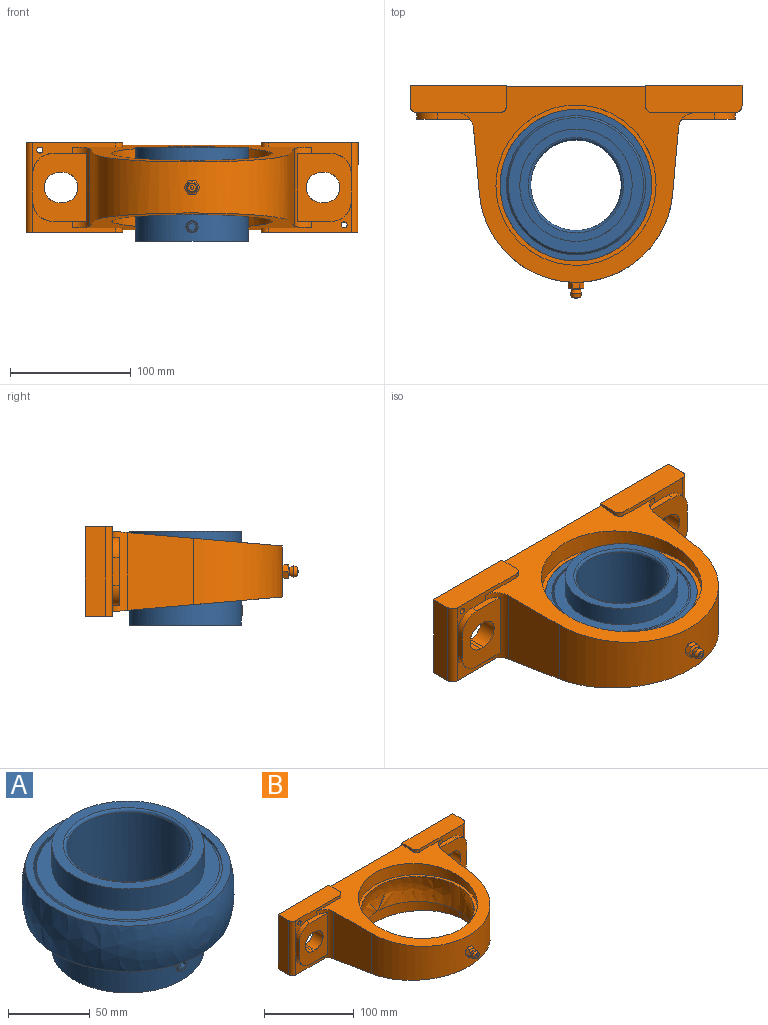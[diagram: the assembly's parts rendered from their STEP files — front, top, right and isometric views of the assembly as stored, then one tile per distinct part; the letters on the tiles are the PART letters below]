
ASSEMBLY  parts=2 mates=1
PART A: 143 faces, bbox 127.1x129.4x131.6 mm
  f0: plane 7.1x6.16mm, normal (0.87,0.5,0), area 38.5mm2, adj f1
  f1: cone r=1.71mm half-angle=45deg, axis (0.87,0.5,0), area 56.6mm2, adj f0,f2
  f2: cylinder r=5mm len=10.05mm, axis (0.87,0.5,0), area 79.3mm2, adj f1,f3
  f3: cylinder r=37.5mm len=75mm, axis (0,0,1), area 17220.6mm2, adj f2,f4,f139,f142
  f4: torus R=39.5mm, axis (0,0,-1), area 754.6mm2, adj f3,f5
  f5: plane 93.01x93.01mm, normal (0,0,-1), area 1887mm2, adj f4,f6
  f6: cylinder r=46.5mm len=93mm, axis (0,0,-1), area 7783.3mm2, adj f5,f7,f105,f106,f107,f108,f109,f110
  f7: sphere r=8.34mm, area 847.9mm2, adj f6,f8,f9,f10,f53,f54,f55,f56
  f8: torus R=51.49mm, axis (0,0,1), area 160.7mm2, adj f7,f9,f95,f106
  f9: torus R=51.49mm, axis (0,0,1), area 160.7mm2, adj f7,f8,f10,f106
  f10: cylinder r=56.49mm len=112.98mm, axis (0,0,1), area 2460.6mm2, adj f7,f9,f11,f13,f15,f17,f19,f21
  f11: torus R=51.49mm, axis (0,0,1), area 160.8mm2, adj f10,f12,f118,f120
  f12: torus R=51.49mm, axis (0,0,1), area 160.7mm2, adj f11,f95,f118,f120
  f13: torus R=51.49mm, axis (0,0,1), area 160.7mm2, adj f10,f14,f116,f118
  f14: torus R=51.49mm, axis (0,0,1), area 160.7mm2, adj f13,f95,f116,f118
  f15: torus R=51.49mm, axis (0,0,1), area 160.7mm2, adj f10,f16,f114,f116
  f16: torus R=51.49mm, axis (0,0,1), area 160.7mm2, adj f15,f95,f114,f116
  f17: torus R=51.49mm, axis (0,0,1), area 160.7mm2, adj f10,f18,f112,f114
  f18: torus R=51.49mm, axis (0,0,1), area 160.7mm2, adj f17,f95,f112,f114
  f19: torus R=51.49mm, axis (0,0,1), area 160.7mm2, adj f10,f20,f110,f112
  f20: torus R=51.49mm, axis (0,0,1), area 160.7mm2, adj f19,f95,f110,f112
  f21: torus R=51.49mm, axis (0,0,1), area 81.7mm2, adj f10,f22,f24,f110
  f22: torus R=51.49mm, axis (0,0,1), area 81.7mm2, adj f21,f23,f95,f110
  f23: torus R=51.49mm, axis (0,0,1), area 78.9mm2, adj f22,f24,f95,f108
  f24: torus R=51.49mm, axis (0,0,1), area 79mm2, adj f10,f21,f23,f108
  f25: torus R=51.49mm, axis (0,0,1), area 160.7mm2, adj f10,f26,f106,f108
  f26: torus R=51.49mm, axis (0,0,1), area 160.7mm2, adj f25,f95,f106,f108
  f27: torus R=51.49mm, axis (0,0,1), area 160.7mm2, adj f10,f28,f135,f137
  f28: torus R=51.49mm, axis (0,0,1), area 160.7mm2, adj f27,f95,f135,f137
  f29: torus R=51.49mm, axis (0,0,1), area 160.7mm2, adj f10,f30,f133,f135
  f30: torus R=51.49mm, axis (0,0,1), area 160.7mm2, adj f29,f95,f133,f135
  f31: torus R=51.49mm, axis (0,0,1), area 160.7mm2, adj f10,f32,f131,f133
  f32: torus R=51.49mm, axis (0,0,1), area 160.7mm2, adj f31,f95,f131,f133
  f33: torus R=51.49mm, axis (0,0,1), area 160.7mm2, adj f10,f34,f129,f131
  f34: torus R=51.49mm, axis (0,0,1), area 160.7mm2, adj f33,f95,f129,f131
  f35: torus R=51.49mm, axis (0,0,1), area 160.7mm2, adj f10,f36,f127,f129
  f36: torus R=51.49mm, axis (0,0,1), area 160.7mm2, adj f35,f95,f127,f129
  f37: torus R=51.49mm, axis (0,0,1), area 160.7mm2, adj f10,f38,f124,f127
  f38: torus R=51.49mm, axis (0,0,1), area 160.7mm2, adj f37,f95,f124,f127
  f39: torus R=51.49mm, axis (0,0,1), area 160.8mm2, adj f10,f40,f122,f124
  f40: torus R=51.49mm, axis (0,0,1), area 160.7mm2, adj f39,f95,f122,f124
  f41: torus R=51.49mm, axis (0,0,1), area 160.8mm2, adj f10,f42,f120,f122
  f42: torus R=51.49mm, axis (0,0,1), area 160.7mm2, adj f41,f95,f120,f122
  f43: cylinder r=0.87mm len=9.02mm, axis (0,-0.97,0.26), area 45.2mm2, adj f10,f44
  f44: sphere r=65mm, area 19597mm2, adj f43,f45
  f45: plane 125.48x125.48mm, normal (0,0,1), area 1907.7mm2, adj f44,f46
  f46: cylinder r=57.62mm len=115.24mm, axis (0,0,1), area 611.8mm2, adj f45,f47
  f47: cone r=55.93mm half-angle=45deg, axis (0,0,1), area 852.6mm2, adj f46,f48
  f48: plane 113.5x113.5mm, normal (0,0,1), area 3025.4mm2, adj f47,f49
  f49: cylinder r=46.51mm len=93.02mm, axis (0,0,-1), area 990.7mm2, adj f48,f50
  f50: plane 115.25x115.25mm, normal (0,0,-1), area 3627.1mm2, adj f49,f51
  f51: cylinder r=57.62mm len=115.24mm, axis (0,0,1), area 3.6mm2, adj f50,f52
  f52: plane 115.25x115.25mm, normal (0,0,1), area 412mm2, adj f10,f51
  f53: torus R=51.49mm, axis (0,0,1), area 160.7mm2, adj f7,f10,f54,f137
  f54: torus R=51.49mm, axis (0,0,1), area 160.7mm2, adj f7,f53,f95,f137
  f55: torus R=51.49mm, axis (0,0,1), area 120.6mm2, adj f7,f56,f137,f138
  f56: cylinder r=46.5mm len=93mm, axis (0,0,-1), area 10888.8mm2, adj f7,f55,f57,f67,f68,f69,f70,f71
  f57: cylinder r=5mm len=10mm, axis (-0.87,-0.5,0), area 4.9mm2, adj f56,f58
  f58: cone r=2.14mm half-angle=45deg, axis (-0.87,-0.5,0), area 37.1mm2, adj f57,f59
  f59: plane 8.28x7.19mm, normal (-0.87,-0.5,0), area 30.7mm2, adj f58,f60,f62,f63,f64,f65,f66
  f60: plane 5.58x4.67mm, normal (-0.25,0.43,0.87), area 14.4mm2, adj f59,f61,f62,f66
  f61: plane 5.77x4.33mm, normal (-0.87,-0.5,0), area 21.7mm2, adj f60,f62,f63,f64,f65,f66
  f62: plane 5.58x4.67mm, normal (0.25,-0.43,0.87), area 14.4mm2, adj f59,f60,f61,f63
  f63: plane 4.33x2.89mm, normal (0.5,-0.87,0), area 14.4mm2, adj f59,f61,f62,f64
  f64: plane 5.58x4.67mm, normal (0.25,-0.43,-0.87), area 14.4mm2, adj f59,f61,f63,f65
  f65: plane 5.58x4.67mm, normal (-0.25,0.43,-0.87), area 14.4mm2, adj f59,f61,f64,f66
  f66: plane 4.33x2.89mm, normal (-0.5,0.87,0), area 14.4mm2, adj f59,f60,f61,f65
  f67: torus R=51.49mm, axis (0,0,1), area 120.6mm2, adj f56,f118,f119,f120
  f68: torus R=51.49mm, axis (0,0,1), area 120.6mm2, adj f56,f116,f117,f118
  f69: torus R=51.49mm, axis (0,0,1), area 120.6mm2, adj f56,f114,f115,f116
  f70: torus R=51.49mm, axis (0,0,1), area 120.6mm2, adj f56,f112,f113,f114
  f71: torus R=51.49mm, axis (0,0,1), area 120.6mm2, adj f56,f110,f111,f112
  f72: torus R=51.49mm, axis (0,0,1), area 120.6mm2, adj f56,f108,f109,f110
  f73: torus R=51.49mm, axis (0,0,1), area 120.6mm2, adj f56,f106,f107,f108
  f74: torus R=51.49mm, axis (0,0,1), area 120.6mm2, adj f56,f135,f136,f137
  f75: torus R=51.49mm, axis (0,0,1), area 120.6mm2, adj f56,f133,f134,f135
  f76: torus R=51.49mm, axis (0,0,1), area 120.6mm2, adj f56,f131,f132,f133
  f77: torus R=51.49mm, axis (0,0,1), area 120.6mm2, adj f56,f129,f130,f131
  f78: torus R=51.49mm, axis (0,0,1), area 120.6mm2, adj f56,f127,f128,f129
  f79: torus R=51.49mm, axis (0,0,1), area 59.1mm2, adj f56,f80,f126,f127
  f80: torus R=51.49mm, axis (0,0,1), area 61.5mm2, adj f56,f79,f124,f125
  f81: torus R=51.49mm, axis (0,0,1), area 120.6mm2, adj f56,f122,f123,f124
  f82: torus R=51.49mm, axis (0,0,1), area 120.6mm2, adj f56,f120,f121,f122
  f83: plane 93.01x93.01mm, normal (0,0,1), area 1887mm2, adj f56,f142
  f84: cylinder r=5mm len=10mm, axis (0,1,0), area 4.9mm2, adj f56,f85
  f85: cone r=4.08mm half-angle=45deg, axis (0,1,0), area 37.1mm2, adj f84,f86
  f86: plane 8.28x8.28mm, normal (0,1,0), area 30.7mm2, adj f85,f87,f89,f90,f91,f92,f93
  f87: plane 5x2.5mm, normal (0.5,0,0.87), area 14.4mm2, adj f86,f88,f89,f93
  f88: plane 5.77x5mm, normal (0,1,0), area 21.7mm2, adj f87,f89,f90,f91,f92,f93
  f89: plane 5x2.5mm, normal (-0.5,0,0.87), area 14.4mm2, adj f86,f87,f88,f90
  f90: plane 5x2.89mm, normal (-1,0,0), area 14.4mm2, adj f86,f88,f89,f91
  f91: plane 5x2.5mm, normal (-0.5,0,-0.87), area 14.4mm2, adj f86,f88,f90,f92
  f92: plane 5x2.5mm, normal (0.5,0,-0.87), area 14.4mm2, adj f86,f88,f91,f93
  f93: plane 5x2.89mm, normal (1,0,0), area 14.4mm2, adj f86,f87,f88,f92
  f94: torus R=51.49mm, axis (0,0,1), area 120.6mm2, adj f7,f56,f105,f106
  f95: cylinder r=56.49mm len=112.98mm, axis (0,0,1), area 2463.2mm2, adj f7,f8,f12,f14,f16,f18,f20,f22
  f96: plane 115.25x115.25mm, normal (0,0,-1), area 397.7mm2, adj f95,f97
  f97: cylinder r=57.62mm len=115.24mm, axis (0,0,1), area 3.6mm2, adj f96,f98
  f98: plane 116.6x116.6mm, normal (0,0,1), area 3638.6mm2, adj f97,f99
  f99: cylinder r=46.51mm len=93.02mm, axis (0,0,1), area 990.7mm2, adj f98,f100
  f100: plane 113.5x113.5mm, normal (0,0,-1), area 3025.4mm2, adj f99,f101
  f101: cone r=55.93mm half-angle=45deg, axis (0,0,-1), area 852.6mm2, adj f100,f102
  f102: cylinder r=57.62mm len=115.24mm, axis (0,0,1), area 611.8mm2, adj f101,f103
  f103: plane 125.48x125.48mm, normal (0,0,-1), area 1909mm2, adj f102,f104
  f104: sphere r=65mm, area 19599.5mm2, adj f103
  f105: torus R=51.49mm, axis (0,0,1), area 120.6mm2, adj f6,f7,f94,f106
  f106: sphere r=8.34mm, area 847.9mm2, adj f6,f8,f9,f10,f25,f26,f56,f73
  f107: torus R=51.49mm, axis (0,0,1), area 120.6mm2, adj f6,f73,f106,f108
  f108: sphere r=8.34mm, area 847.9mm2, adj f6,f10,f23,f24,f25,f26,f56,f72
  f109: torus R=51.49mm, axis (0,0,1), area 120.6mm2, adj f6,f72,f108,f110
  f110: sphere r=8.34mm, area 847.9mm2, adj f6,f10,f19,f20,f21,f22,f56,f71
  f111: torus R=51.49mm, axis (0,0,1), area 120.6mm2, adj f6,f71,f110,f112
  f112: sphere r=8.34mm, area 847.9mm2, adj f6,f10,f17,f18,f19,f20,f56,f70
  f113: torus R=51.49mm, axis (0,0,1), area 120.6mm2, adj f6,f70,f112,f114
  f114: sphere r=8.34mm, area 847.9mm2, adj f6,f10,f15,f16,f17,f18,f56,f69
  f115: torus R=51.49mm, axis (0,0,1), area 120.6mm2, adj f6,f69,f114,f116
  f116: sphere r=8.34mm, area 847.9mm2, adj f6,f10,f13,f14,f15,f16,f56,f68
  f117: torus R=51.49mm, axis (0,0,1), area 120.6mm2, adj f6,f68,f116,f118
  f118: sphere r=8.34mm, area 847.9mm2, adj f6,f10,f11,f12,f13,f14,f56,f67
  f119: torus R=51.49mm, axis (0,0,1), area 120.6mm2, adj f6,f67,f118,f120
  f120: sphere r=8.34mm, area 847.9mm2, adj f6,f10,f11,f12,f41,f42,f56,f67
  f121: torus R=51.49mm, axis (0,0,1), area 120.6mm2, adj f6,f82,f120,f122
  f122: sphere r=8.34mm, area 847.9mm2, adj f6,f10,f39,f40,f41,f42,f56,f81
  f123: torus R=51.49mm, axis (0,0,1), area 120.6mm2, adj f6,f81,f122,f124
  f124: sphere r=8.34mm, area 847.9mm2, adj f6,f10,f37,f38,f39,f40,f56,f80
  f125: torus R=51.49mm, axis (0,0,1), area 61.5mm2, adj f6,f80,f124,f126
  f126: torus R=51.49mm, axis (0,0,1), area 59.1mm2, adj f6,f79,f125,f127
  f127: sphere r=8.34mm, area 847.9mm2, adj f6,f10,f35,f36,f37,f38,f56,f78
  f128: torus R=51.49mm, axis (0,0,1), area 120.6mm2, adj f6,f78,f127,f129
  f129: sphere r=8.34mm, area 847.9mm2, adj f6,f10,f33,f34,f35,f36,f56,f77
  f130: torus R=51.49mm, axis (0,0,1), area 120.6mm2, adj f6,f77,f129,f131
  f131: sphere r=8.34mm, area 847.9mm2, adj f6,f10,f31,f32,f33,f34,f56,f76
  f132: torus R=51.49mm, axis (0,0,1), area 120.6mm2, adj f6,f76,f131,f133
  f133: sphere r=8.34mm, area 847.9mm2, adj f6,f10,f29,f30,f31,f32,f56,f75
  f134: torus R=51.49mm, axis (0,0,1), area 120.6mm2, adj f6,f75,f133,f135
  f135: sphere r=8.34mm, area 847.9mm2, adj f6,f10,f27,f28,f29,f30,f56,f74
  f136: torus R=51.49mm, axis (0,0,1), area 120.6mm2, adj f6,f74,f135,f137
  f137: sphere r=8.34mm, area 847.9mm2, adj f6,f10,f27,f28,f53,f54,f55,f56
  f138: torus R=51.49mm, axis (0,0,1), area 120.6mm2, adj f6,f7,f55,f137
  f139: cylinder r=5mm len=10mm, axis (0,-1,0), area 79.3mm2, adj f3,f140
  f140: cone r=3.5mm half-angle=45deg, axis (0,-1,0), area 56.6mm2, adj f139,f141
  f141: plane 7.1x7.1mm, normal (0,-1,0), area 38.5mm2, adj f140
  f142: torus R=39.5mm, axis (0,0,-1), area 754.6mm2, adj f3,f83
PART B: 85 faces, bbox 315.1x216.6x170.1 mm
  f0: plane 65.39x49.89mm, normal (0,1,0), area 2651.8mm2, adj f8,f9,f10,f11,f13,f14,f15,f16
  f1: plane 65.39x49.89mm, normal (0,1,0), area 2651.8mm2, adj f3,f4,f5,f6,f18,f19,f20,f21
  f2: sphere r=65.01mm, area 12961.5mm2, adj f24,f27
  f3: plane 49.5x12.6mm, normal (1,0,0), area 623.7mm2, adj f1,f4,f6,f31
  f4: plane 65x12.6mm, normal (0,0,1), area 819mm2, adj f1,f3,f5,f31
  f5: plane 49.5x12.6mm, normal (-1,0,0), area 623.7mm2, adj f1,f4,f6,f31
  f6: plane 65x12.6mm, normal (0,0,-1), area 819mm2, adj f1,f3,f5,f31
  f7: plane 74x16.8mm, normal (1,0,0), area 1243.2mm2, adj f29,f30,f31,f32
  f8: plane 49.5x12.6mm, normal (1,0,0), area 623.7mm2, adj f0,f9,f11,f33
  f9: plane 65x12.6mm, normal (0,0,1), area 819mm2, adj f0,f8,f10,f33
  f10: plane 49.5x12.6mm, normal (-1,0,0), area 623.7mm2, adj f0,f9,f11,f33
  f11: plane 65x12.6mm, normal (0,0,-1), area 819mm2, adj f0,f8,f10,f33
  f12: plane 74x16.8mm, normal (-1,0,0), area 1243.2mm2, adj f33,f34,f35,f36
  f13: plane 15.4x3mm, normal (0,0,1), area 46.2mm2, adj f0,f14,f16,f39
  f14: cylinder r=12.5mm len=25mm, axis (0,-1,0), area 604.8mm2, adj f0,f13,f15,f39
  f15: plane 15.4x3mm, normal (0,0,-1), area 46.2mm2, adj f0,f14,f16,f39
  f16: cylinder r=12.5mm len=25mm, axis (0,-1,0), area 604.8mm2, adj f0,f13,f15,f39
  f17: plane 22.52x5.6mm, normal (-1,0,0), area 126.1mm2, adj f26,f36,f37,f39
  f18: plane 15.4x3mm, normal (0,0,1), area 46.2mm2, adj f1,f19,f21,f42
  f19: cylinder r=12.5mm len=25mm, axis (0,-1,0), area 604.8mm2, adj f1,f18,f20,f42
  f20: plane 15.4x3mm, normal (0,0,-1), area 46.2mm2, adj f1,f19,f21,f42
  f21: cylinder r=12.5mm len=25mm, axis (0,-1,0), area 604.8mm2, adj f1,f18,f20,f42
  f22: plane 22.52x5.6mm, normal (1,0,0), area 126.1mm2, adj f25,f28,f29,f42
  f23: sphere r=2.11mm, area 8.9mm2, adj f44
  f24: plane 172.74x172.74mm, normal (0,0,-1), area 1506mm2, adj f2,f45,f46
  f25: cylinder r=16.89mm len=16.89mm, axis (0,1,0), area 148.6mm2, adj f22,f41,f42,f47
  f26: cylinder r=16.89mm len=16.89mm, axis (0,1,0), area 148.6mm2, adj f17,f39,f40,f48
  f27: plane 172.74x172.74mm, normal (0,0,1), area 1506mm2, adj f2,f51
  f28: cylinder r=16.89mm len=16.89mm, axis (0,1,0), area 148.6mm2, adj f22,f42,f43,f52
  f29: cylinder r=5.6mm len=74mm, axis (0,0,1), area 650.9mm2, adj f7,f22,f30,f32,f47,f52
  f30: plane 80.35x22.75mm, normal (0,0,1), area 1778.7mm2, adj f7,f29,f31,f52,f53,f54
  f31: plane 80x74mm, normal (0,1,0), area 2682.9mm2, adj f3,f4,f5,f6,f7,f30,f32,f54
  f32: plane 80.35x22.75mm, normal (0,0,-1), area 1778.5mm2, adj f7,f29,f31,f47,f50,f54
  f33: plane 80x74mm, normal (0,1,0), area 2682.9mm2, adj f8,f9,f10,f11,f12,f34,f35,f56
  f34: plane 80.35x22.75mm, normal (0,0,-1), area 1778.7mm2, adj f12,f33,f36,f48,f49,f56
  f35: plane 80.35x22.75mm, normal (0,0,1), area 1778.5mm2, adj f12,f33,f36,f56,f57,f58
  f36: cylinder r=5.6mm len=74mm, axis (0,0,1), area 650.9mm2, adj f12,f17,f34,f35,f48,f58
  f37: cylinder r=16.89mm len=16.89mm, axis (0,1,0), area 148.6mm2, adj f17,f38,f39,f58
  f38: plane 27.73x5.93mm, normal (0,0,1), area 134.6mm2, adj f37,f39,f58,f59
  f39: plane 56.3x44.3mm, normal (0,-1,0), area 1805.6mm2, adj f13,f14,f15,f16,f17,f26,f37,f38
  f40: plane 27.74x5.93mm, normal (0,0,-1), area 134.6mm2, adj f26,f39,f48,f59
  f41: plane 27.65x5.84mm, normal (0,0,-1), area 134.6mm2, adj f25,f42,f47,f61
  f42: plane 56.3x44.3mm, normal (0,-1,0), area 1805.6mm2, adj f18,f19,f20,f21,f22,f25,f28,f41
  f43: plane 27.65x5.84mm, normal (0,0,1), area 134.6mm2, adj f28,f42,f52,f61
  f44: plane 7.06x7.06mm, normal (0,-1,0), area 30.6mm2, adj f23,f62
  f45: cylinder r=66.31mm len=132.62mm, axis (0,0,1), area 3063mm2, adj f24,f46,f63
  f46: cylinder r=66.31mm len=132.62mm, axis (0,0,1), area 1706.5mm2, adj f24,f45,f63
  f47: plane 68.8x25.74mm, normal (0,-1,0), area 468.3mm2, adj f25,f29,f32,f41,f50,f61,f63,f84
  f48: plane 68.8x25.74mm, normal (0,-1,0), area 487.9mm2, adj f26,f34,f36,f40,f49,f59,f63
  f49: cylinder r=5.6mm len=5.6mm, axis (0,0,1), area 30.8mm2, adj f34,f48,f56,f63
  f50: cylinder r=5.6mm len=5.6mm, axis (0,0,-1), area 30.8mm2, adj f32,f47,f54,f63
  f51: cylinder r=66.31mm len=132.62mm, axis (0,0,-1), area 4442.1mm2, adj f27,f65
  f52: plane 68.8x25.74mm, normal (0,-1,0), area 487.9mm2, adj f28,f29,f30,f43,f53,f61,f65
  f53: cylinder r=5.6mm len=5.6mm, axis (0,0,-1), area 30.8mm2, adj f30,f52,f54,f65
  f54: plane 74x16.8mm, normal (-1,0,0), area 164mm2, adj f30,f31,f32,f50,f53,f55,f63,f65
  f55: plane 115x70.18mm, normal (0,1,0), area 8070.8mm2, adj f54,f56,f63,f65
  f56: plane 74x16.8mm, normal (1,0,0), area 164mm2, adj f33,f34,f35,f49,f55,f57,f63,f65
  f57: cylinder r=5.6mm len=5.6mm, axis (0,0,1), area 30.8mm2, adj f35,f56,f58,f65
  f58: plane 68.8x25.74mm, normal (0,-1,0), area 468.3mm2, adj f35,f36,f37,f38,f57,f59,f65,f83
  f59: cylinder r=14mm len=66.51mm, axis (0,0,-1), area 627.5mm2, adj f38,f39,f40,f48,f58,f60,f63,f65
  f60: plane 64.3x54.43mm, normal (-1,-0.09,0), area 3256.2mm2, adj f59,f63,f65,f67
  f61: cylinder r=14mm len=66.51mm, axis (0,0,-1), area 627.5mm2, adj f41,f42,f43,f47,f52,f63,f64,f65
  f62: cone r=4.62mm half-angle=20deg, axis (0,1,0), area 84.4mm2, adj f44,f66
  f63: plane 205.48x169.85mm, normal (0,-0.09,-1), area 8924.4mm2, adj f45,f46,f47,f48,f49,f50,f54,f55
  f64: plane 64.3x54.43mm, normal (1,-0.09,0), area 3256.2mm2, adj f61,f63,f65,f67
  f65: plane 205.48x169.85mm, normal (0,-0.09,1), area 8912mm2, adj f51,f52,f53,f54,f55,f56,f57,f58
  f66: cone r=4.62mm half-angle=15deg, axis (0,-1,0), area 95.9mm2, adj f62,f71
  f67: cylinder r=80.4mm len=160.19mm, axis (0,0,1), area 12121.7mm2, adj f60,f63,f64,f65,f74
  f68: plane 7.55x7.01mm, normal (0.87,0,-0.5), area 30.1mm2, adj f69,f71,f72,f77,f78
  f69: plane 8.41x7.01mm, normal (0,0,-1), area 30.1mm2, adj f68,f70,f71,f78,f79
  f70: plane 7.55x7.01mm, normal (-0.87,0,-0.5), area 30.1mm2, adj f69,f71,f73,f75,f79
  f71: cone r=3.66mm half-angle=60deg, axis (0,1,0), area 101mm2, adj f66,f68,f69,f70,f72,f73,f80
  f72: plane 7.55x7.01mm, normal (0.87,0,0.5), area 30.1mm2, adj f68,f71,f76,f77,f80
  f73: plane 7.55x7.01mm, normal (-0.87,0,0.5), area 30.1mm2, adj f70,f71,f75,f80,f82
  f74: cylinder r=3.98mm len=7.96mm, axis (0,1,0), area 1.5mm2, adj f67,f81
  f75: cone r=5.56mm half-angle=60deg, axis (0,-1,0), area 3mm2, adj f70,f73,f81
  f76: cone r=5.56mm half-angle=60deg, axis (0,-1,0), area 3mm2, adj f72,f80,f81
  f77: cone r=5.56mm half-angle=60deg, axis (0,-1,0), area 3mm2, adj f68,f72,f81
  f78: cone r=5.56mm half-angle=60deg, axis (0,-1,0), area 2.6mm2, adj f68,f69,f81
  f79: cone r=5.56mm half-angle=60deg, axis (0,-1,0), area 3mm2, adj f69,f70,f81
  f80: plane 8.41x7.01mm, normal (0,0,1), area 30.1mm2, adj f71,f72,f73,f76,f82
  f81: plane 11.3x11.3mm, normal (0,1,0), area 47.5mm2, adj f74,f75,f76,f77,f78,f79,f82
  f82: cone r=5.56mm half-angle=60deg, axis (0,-1,0), area 2.6mm2, adj f73,f80,f81
  f83: cylinder r=2.5mm len=22.4mm, axis (0,-1,0), area 351.9mm2, adj f33,f58
  f84: cylinder r=2.5mm len=22.4mm, axis (0,-1,0), area 351.9mm2, adj f31,f47
PLACE A t=(-1,42,0.7)mm
PLACE B t=(-1,42,0.7)mm
MATE fastened A.f121 <-> B.f45  axis (0,0,-1) through (107.5,-40.6,-43.8)mm
